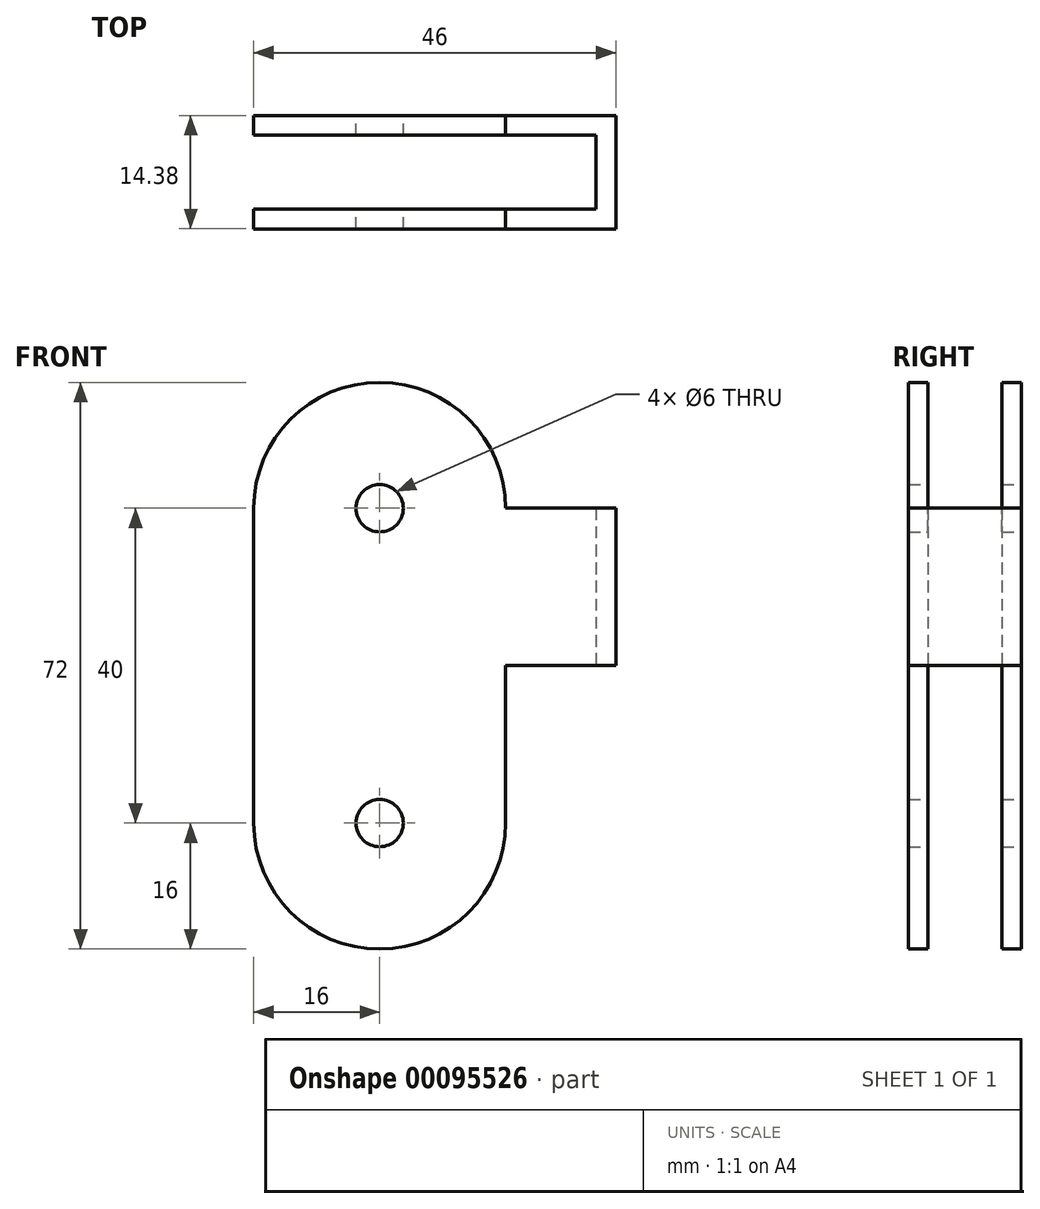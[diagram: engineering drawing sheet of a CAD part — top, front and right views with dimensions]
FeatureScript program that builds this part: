
annotation { "Feature Type Name" : "Feature", "Feature Type Description" : "" }
export const myFeature = defineFeature(function(context is Context, id is Id, definition is map)
    precondition{}
    {
        {
            var Q0;
            Q0=qCreatedBy(makeId("Front.planeOp"),FACE);
            var sketch = newSketch(context, id + "F0", { "sketchPlane" : qUnion([Q0])});
            skLineSegment(sketch, "E0", {"start": v(-16, 0) * mm, "end": v(-16, 20) * mm});
            skArc(sketch, "E1", {"start": v(0, 36) * mm, "mid": v(-11.31, 31.31) * mm, "end": v(-16, 20) * mm});
            skArc(sketch, "E2.MirrorCS", {"start": v(0, 36) * mm, "mid": v(11.31, 31.31) * mm, "end": v(16, 20) * mm});
            skArc(sketch, "E3.MirrorCS", {"start": v(0, -36) * mm, "mid": v(11.31, -31.31) * mm, "end": v(16, -20) * mm});
            skArc(sketch, "E4.MirrorCS", {"start": v(0, -36) * mm, "mid": v(-11.31, -31.31) * mm, "end": v(-16, -20) * mm});
            skLineSegment(sketch, "E5.MirrorCS", {"start": v(16, 0) * mm, "end": v(16, -20) * mm});
            skLineSegment(sketch, "E6.MirrorCS", {"start": v(-16, 0) * mm, "end": v(-16, -20) * mm});
            skCircle(sketch, "E7", {"center": v(0, 20) * mm, "radius": 3 * mm});
            skCircle(sketch, "E8", {"center": v(0, -20) * mm, "radius": 3 * mm});
            skPoint(sketch, "E9.MirrorCS.end.orphan", {"position": v(16, 20) * mm});
            skPoint(sketch, "E9.MirrorCS.start.orphan", {"position": v(16, 0) * mm});
            skLineSegment(sketch, "E10", {"start": v(16, 20) * mm, "end": v(30, 20) * mm});
            skLineSegment(sketch, "E11", {"start": v(16, 0) * mm, "end": v(30, 0) * mm});
            skLineSegment(sketch, "E12", {"start": v(30, 20) * mm, "end": v(30, 0) * mm});
            skSolve(sketch);
        }
        {
            var Q0;
            Q0=makeQuery(id+"F0.imprint","IMPRINT",FACE,{"disambiguationData":[TD([[makeQuery(id+"F0.imprint","IMPRINT",EDGE,{"derivedFrom":sQuery(id+"F0.wireOp",EDGE,"E0")}),-1.0]])]});
            extrude(context, id + "F1", {"entities" : qUnion([Q0]), "depth" : 14.38 * mm});
        }
        {
            var Q0;
            Q0=makeQuery(id+"F1.opExtrude","SWEPT_FACE",FACE,{"disambiguationData":[OSD([sQuery(id+"F0.wireOp",EDGE,"E5.MirrorCS")])]});
            var Q1;
            Q1=makeQuery(id+"F1.opExtrude","SWEPT_FACE",FACE,{"disambiguationData":[OSD([sQuery(id+"F0.wireOp",EDGE,"E0"),sQuery(id+"F0.wireOp",EDGE,"E6.MirrorCS")])]});
            var Q2;
            Q2=makeQuery(id+"F1.opExtrude","SWEPT_FACE",FACE,{"disambiguationData":[OSD([sQuery(id+"F0.wireOp",EDGE,"E11")])]});
            var Q3;
            Q3=makeQuery(id+"F1.opExtrude","SWEPT_FACE",FACE,{"disambiguationData":[OSD([sQuery(id+"F0.wireOp",EDGE,"E3.MirrorCS"),sQuery(id+"F0.wireOp",EDGE,"E4.MirrorCS")])]});
            var Q4;
            Q4=makeQuery(id+"F1.opExtrude","SWEPT_FACE",FACE,{"disambiguationData":[OSD([sQuery(id+"F0.wireOp",EDGE,"E8")])]});
            var Q5;
            Q5=makeQuery(id+"F1.opExtrude","SWEPT_FACE",FACE,{"disambiguationData":[OSD([sQuery(id+"F0.wireOp",EDGE,"E7")])]});
            var Q6;
            Q6=makeQuery(id+"F1.opExtrude","SWEPT_FACE",FACE,{"disambiguationData":[OSD([sQuery(id+"F0.wireOp",EDGE,"E1"),sQuery(id+"F0.wireOp",EDGE,"E2.MirrorCS")])]});
            var Q7;
            Q7=makeQuery(id+"F1.opExtrude","SWEPT_FACE",FACE,{"disambiguationData":[OSD([sQuery(id+"F0.wireOp",EDGE,"E10")])]});
            shell(context, id + "F2", {"entities" : qUnion([Q0, Q1, Q2, Q3, Q4, Q5, Q6, Q7]), "thickness" : 2.5 * mm});
        }
    });
